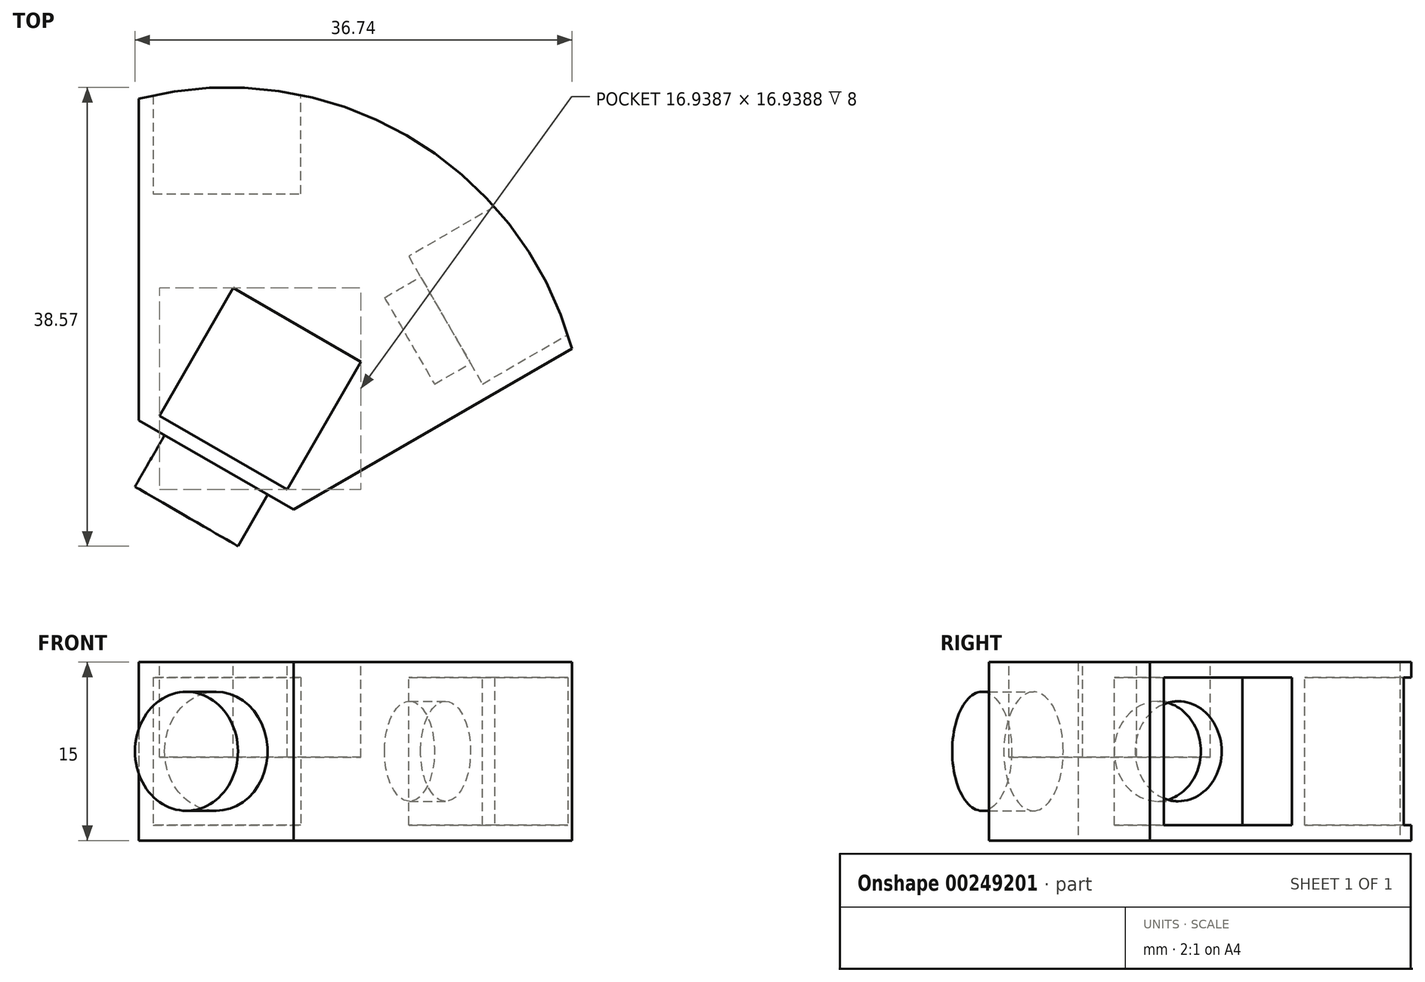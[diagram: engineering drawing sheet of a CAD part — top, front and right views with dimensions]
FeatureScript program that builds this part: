
annotation { "Feature Type Name" : "Feature", "Feature Type Description" : "" }
export const myFeature = defineFeature(function(context is Context, id is Id, definition is map)
    precondition{}
    {
        {
            var Q0;
            Q0=qCreatedBy(makeId("Top.planeOp"),FACE);
            var sketch = newSketch(context, id + "F0", { "sketchPlane" : qUnion([Q0])});
            skCircle(sketch, "E0", {"center": v(0, 0) * mm, "radius": 30 * mm});
            skLineSegment(sketch, "E1.bottom", {"start": v(7.5, 39.48) * mm, "end": v(-7.5, 39.48) * mm});
            skLineSegment(sketch, "E1.top", {"start": v(7.5, -39.48) * mm, "end": v(-7.5, -39.48) * mm});
            skLineSegment(sketch, "E1.left", {"start": v(7.5, 39.48) * mm, "end": v(7.5, -39.48) * mm});
            skLineSegment(sketch, "E1.right", {"start": v(-7.5, 39.48) * mm, "end": v(-7.5, -39.48) * mm});
            skLineSegment(sketch, "E2.1.0", {"start": v(-30.44, -26.24) * mm, "end": v(37.94, 13.25) * mm});
            skLineSegment(sketch, "E2.1.1", {"start": v(-37.94, -13.25) * mm, "end": v(30.44, 26.24) * mm});
            skLineSegment(sketch, "E2.2.0", {"start": v(37.94, -13.25) * mm, "end": v(-30.44, 26.24) * mm});
            skLineSegment(sketch, "E2.2.1", {"start": v(30.44, -26.24) * mm, "end": v(-37.94, 13.25) * mm});
            skLineSegment(sketch, "E3", {"start": v(-7.5, 2) * mm, "end": v(5.5, -5.5) * mm});
            skSolve(sketch);
        }
        {
            var Q0;
            {var subQ1=sQuery(id+"F0.wireOp",EDGE,"E0");var subQ5=sQuery(id+"F0.wireOp",EDGE,"E1.left");var subQ6=makeQuery(id+"F0.imprint","INTERSECT",VERTEX,{"disambiguationData":[OD(0.0)],"derivedFrom":[subQ1,subQ5]});Q0=makeQuery(id+"F0.imprint","IMPRINT",FACE,{"disambiguationData":[TD([[makeQuery(id+"F0.imprint","IMPRINT",EDGE,{"disambiguationData":[TD([[subQ6,-1.0]])],"derivedFrom":subQ1}),1.0]])]});}
            var Q1;
            {var subQ0=sQuery(id+"F0.wireOp",EDGE,"E2.1.1");var subQ1=sQuery(id+"F0.wireOp",EDGE,"E0");var subQ2=makeQuery(id+"F0.imprint","INTERSECT",VERTEX,{"disambiguationData":[OD(0.0)],"derivedFrom":[subQ1,subQ0]});Q1=makeQuery(id+"F0.imprint","IMPRINT",FACE,{"disambiguationData":[TD([[makeQuery(id+"F0.imprint","IMPRINT",EDGE,{"disambiguationData":[TD([[subQ2,-1.0]])],"derivedFrom":subQ1}),1.0]])]});}
            var Q2;
            {var subQ1=sQuery(id+"F0.wireOp",EDGE,"E0");var subQ5=sQuery(id+"F0.wireOp",EDGE,"E2.1.1");var subQ6=makeQuery(id+"F0.imprint","INTERSECT",VERTEX,{"disambiguationData":[OD(0.0)],"derivedFrom":[subQ1,subQ5]});Q2=makeQuery(id+"F0.imprint","IMPRINT",FACE,{"disambiguationData":[TD([[makeQuery(id+"F0.imprint","IMPRINT",EDGE,{"disambiguationData":[TD([[subQ6,1.0]])],"derivedFrom":subQ1}),1.0]])]});}
            var Q3;
            {var subQ0=sQuery(id+"F0.wireOp",EDGE,"E2.2.0");var subQ1=sQuery(id+"F0.wireOp",EDGE,"E1.left");var subQ2=makeQuery(id+"F0.imprint","INTERSECT",VERTEX,{"derivedFrom":[subQ1,subQ0]});Q3=makeQuery(id+"F0.imprint","IMPRINT",FACE,{"disambiguationData":[TD([[makeQuery(id+"F0.imprint","IMPRINT",EDGE,{"disambiguationData":[TD([[subQ2,-1.0]])],"derivedFrom":subQ1}),1.0]])]});}
            var Q4;
            {var subQ0=sQuery(id+"F0.wireOp",EDGE,"E2.1.1");var subQ1=sQuery(id+"F0.wireOp",EDGE,"E1.left");var subQ2=makeQuery(id+"F0.imprint","INTERSECT",VERTEX,{"derivedFrom":[subQ1,subQ0]});Q4=makeQuery(id+"F0.imprint","IMPRINT",FACE,{"disambiguationData":[TD([[makeQuery(id+"F0.imprint","IMPRINT",EDGE,{"disambiguationData":[TD([[subQ2,-1.0]])],"derivedFrom":subQ1}),-1.0]])]});}
            var Q5;
            {var subQ5=sQuery(id+"F0.wireOp",EDGE,"E3");Q5=makeQuery(id+"F0.imprint","IMPRINT",FACE,{"disambiguationData":[TD([[makeQuery(id+"F0.imprint","IMPRINT",EDGE,{"derivedFrom":subQ5}),1.0]])]});}
            var Q6;
            {var subQ0=sQuery(id+"F0.wireOp",EDGE,"E2.2.0");var subQ1=sQuery(id+"F0.wireOp",EDGE,"E1.right");var subQ2=makeQuery(id+"F0.imprint","INTERSECT",VERTEX,{"derivedFrom":[subQ1,subQ0]});Q6=makeQuery(id+"F0.imprint","IMPRINT",FACE,{"disambiguationData":[TD([[makeQuery(id+"F0.imprint","IMPRINT",EDGE,{"disambiguationData":[TD([[subQ2,-1.0]])],"derivedFrom":subQ1}),1.0]])]});}
            extrude(context, id + "F1", {"entities" : qUnion([Q0, Q1, Q2, Q3, Q4, Q5, Q6]), "depth" : 15 * mm});
        }
        {
            var Q0;
            Q0=makeQuery(id+"F1.opExtrude","CAP_FACE",FACE,{"disambiguationData":[OSD([sQuery(id+"F0.wireOp",EDGE,"E0"),sQuery(id+"F0.wireOp",EDGE,"E1.right"),sQuery(id+"F0.wireOp",EDGE,"E2.1.0"),sQuery(id+"F0.wireOp",EDGE,"E3")])],"isStart":false});
            var sketch = newSketch(context, id + "F2", { "sketchPlane" : qUnion([Q0])});
            skLineSegment(sketch, "E4", {"start": v(-1, -1.74) * mm, "end": v(15, 25.98) * mm});
            skLineSegment(sketch, "E5", {"start": v(-0.4, -0.7) * mm, "end": v(-5.77, 2.4) * mm});
            skLineSegment(sketch, "E6", {"start": v(-5.77, 2.4) * mm, "end": v(0.43, 13.14) * mm});
            skLineSegment(sketch, "E7", {"start": v(0.43, 13.14) * mm, "end": v(11.16, 6.94) * mm});
            skLineSegment(sketch, "E8", {"start": v(11.16, 6.94) * mm, "end": v(4.96, -3.8) * mm});
            skLineSegment(sketch, "E9", {"start": v(-0.4, -0.7) * mm, "end": v(4.96, -3.8) * mm});
            skSolve(sketch);
        }
        {
            var Q0;
            Q0 = qSketchRegion(id + "F2", true);
            extrude(context, id + "F3", {"entities" : qUnion([Q0]), "operationType" : NewBodyOperationType.REMOVE, "oppositeDirection" : true, "depth" : 8 * mm});
        }
        {
            var Q0;
            Q0=makeQuery(id+"F1.opExtrude","CAP_FACE",FACE,{"disambiguationData":[OSD([sQuery(id+"F0.wireOp",EDGE,"E0"),sQuery(id+"F0.wireOp",EDGE,"E1.right"),sQuery(id+"F0.wireOp",EDGE,"E2.1.0"),sQuery(id+"F0.wireOp",EDGE,"E3")])],"isStart":false});
            var sketch = newSketch(context, id + "F4", { "sketchPlane" : qUnion([Q0])});
            skLineSegment(sketch, "E10", {"start": v(-6.3, 31.7) * mm, "end": v(-6.3, 21.05) * mm});
            skLineSegment(sketch, "E11", {"start": v(-6.3, 21.05) * mm, "end": v(6.1, 21.05) * mm});
            skLineSegment(sketch, "E12", {"start": v(6.1, 21.05) * mm, "end": v(6.1, 37.22) * mm});
            skLineSegment(sketch, "E13", {"start": v(-6.3, 31.7) * mm, "end": v(7.98, 31.7) * mm});
            skLineSegment(sketch, "E14", {"start": v(16.18, 2.07) * mm, "end": v(35.93, 13.47) * mm});
            skLineSegment(sketch, "E15", {"start": v(35.93, 13.47) * mm, "end": v(29.73, 24.2) * mm});
            skLineSegment(sketch, "E16", {"start": v(29.73, 24.2) * mm, "end": v(15.18, 15.8) * mm});
            skLineSegment(sketch, "E17", {"start": v(15.18, 15.8) * mm, "end": v(21.38, 5.07) * mm});
            skSolve(sketch);
        }
        {
            var Q0;
            Q0 = qSketchRegion(id + "F4", true);
            extrude(context, id + "F5", {"entities" : qUnion([Q0]), "operationType" : NewBodyOperationType.REMOVE, "oppositeDirection" : true, "depth" : (15 - 1.3) * mm, "hasSecondDirection" : true, "secondDirectionOppositeDirection" : true, "secondDirectionDepth" : 1.3 * mm});
        }
        {
            var Q0;
            Q0=makeQuery(id+"F1.opExtrude","SWEPT_FACE",FACE,{"disambiguationData":[OSD([sQuery(id+"F0.wireOp",EDGE,"E3")])]});
            var sketch = newSketch(context, id + "F6", { "sketchPlane" : qUnion([Q0])});
            skCircle(sketch, "E18", {"center": v(0, 7.5) * mm, "radius": 5 * mm});
            skPoint(sketch, "E18.centerSnap0", {"position": v(-7.5, 7.5) * mm});
            skSolve(sketch);
        }
        {
            var Q0;
            Q0 = qSketchRegion(id + "F6", true);
            extrude(context, id + "F7", {"entities" : qUnion([Q0]), "operationType" : NewBodyOperationType.ADD, "depth" : 5 * mm});
        }
        {
            var Q0;
            Q0=makeQuery(id+"F5.boolean.opBoolean","COPY",FACE,{"derivedFrom":makeQuery(id+"F5.opExtrude","SWEPT_FACE",FACE,{"disambiguationData":[OSD([sQuery(id+"F4.wireOp",EDGE,"E17")])]})});
            var sketch = newSketch(context, id + "F8", { "sketchPlane" : qUnion([Q0])});
            skCircle(sketch, "E19", {"center": v(-0.1, 7.5) * mm, "radius": 4.2 * mm});
            skPoint(sketch, "E19.centerSnap0", {"position": v(-0.1, 1.3) * mm});
            skPoint(sketch, "E19.centerSnap1", {"position": v(6.1, 7.5) * mm});
            skSolve(sketch);
        }
        {
            var Q0;
            Q0 = qSketchRegion(id + "F8", true);
            extrude(context, id + "F9", {"entities" : qUnion([Q0]), "operationType" : NewBodyOperationType.REMOVE, "oppositeDirection" : true, "depth" : 3.5 * mm});
        }
    });
